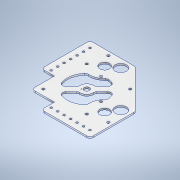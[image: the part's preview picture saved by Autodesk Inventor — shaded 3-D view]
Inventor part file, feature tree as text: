
AUTODESK INVENTOR PART (.ipt)
format: ipt  version: 2020 (Build 240168000, 168)  size: 381,952 bytes
history: native  units: in
note: dims shown in document units (in); Inventor stores cm internally (conversion verified against a paired STEP export)
features: sketch x6, extrude x5, hole x2, fillet x2, chamfer x1
ambient origin geometry x8: Origin, YZ Plane, XZ Plane, XY Plane, X Axis, Y Axis, Z Axis, Center Point
bodies: Solid1 (feature_tree)
feature tree (16):
  extrude  "Extrusion1"  Depth=0.125in TaperAngle=0.0deg
  hole  "Hole1"  [1 undecoded]
  sketch  "Sketch3"  dims[d5=4.25in d9=4.75in]
  extrude  "Extrusion5"  Depth=4.75in
  extrude  "Extrusion6"  Depth=1.0in
  extrude  "Extrusion7"  Depth=6.5in
  chamfer  "Chamfer3"  Distance=2.7272in
  fillet  "Fillet6"  Radius=0.875in
  hole  "Hole2"  [1 undecoded]
  extrude  "Extrusion8"  Depth=0.25in
  fillet  "Fillet7"  Radius=0.375in
  sketch  "Sketch1"  dims[d0=3.0in d1=0.125in d2=0.0in]
  sketch  "Sketch2"  dims[d3=1.0in d4=1.0in]
  sketch  "Sketch5"  dims[d10=0.196in d11=0.75in d12=0.5in d13=0.188in d14=0.5635in d15=1.0in d16=0.8108in d17=4.25in]
  sketch  "Sketch6"  dims[d19=0.75in d25=6.5in]
  sketch  "Sketch7"  dims[d33=1.8in d34=2.7272in d35=0.875in d37=2.0in d38=2.362in d39=0.375in d52=0.196in d53=90.0deg d56=90.0deg d59=0.0in d60=0.0in d61=1.0in d62=0.0in d63=1.0in d64=2.75in d65=1.75in d66=1.0in d67=1.0in d68=0.0in d73=3.0in d74=0.125in d75=45.0deg d76=0.25in d77=0.5in d78=0.5in d79=4.7244in d81=0.5in d82=0.3937in d84=1.0in d86=4.7244in d88=0.5in d89=0.3937in d91=1.0in d93=0.163in d94=0.75in d95=0.375in d96=0.25in d97=0.5635in d98=0.625in d99=0.0in d100=1.0in d102=0.5in d103=1.0in d104=0.0in d105=0.25in d106=0.406in d107=0.062in d108=0.29in]
note: 2 required parameter values undecoded (feature->parameter linkage not recoverable at this tier; creation-order binding heuristic only, values carry confidence <= 0.55)
